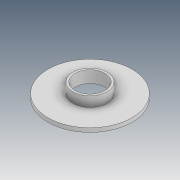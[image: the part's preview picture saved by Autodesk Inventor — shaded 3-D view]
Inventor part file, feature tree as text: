
AUTODESK INVENTOR PART (.ipt)
format: ipt  version: 2020 (Build 240168000, 168)  size: 118,784 bytes
history: native  units: mm
features: revolve x1, sketch x1
ambient origin geometry x8: Origin, YZ Plane, XZ Plane, XY Plane, X Axis, Y Axis, Z Axis, Center Point
bodies: Body1 (feature_tree)
feature tree (2):
  revolve  "Revolution2"  [1 undecoded]
  sketch  "Sketch1"  dims[d0=1.5mm d1=1.5mm d2=20.0mm d3=1.5mm d4=14.5mm d6=8.5mm d7=1.0mm d8=6.0mm d9=1.0mm d10=1.0mm d11=1.0mm d13=0.5mm d14=90.0deg]
note: 1 required parameter value undecoded (feature->parameter linkage not recoverable at this tier; creation-order binding heuristic only, values carry confidence <= 0.55)
